# Revit family: Haworth_Masters_StackOnStorage
name_source: partatom
category: Furniture Systems
revit_build: Autodesk Revit 2018 (Build: 20170223_1515(x64)
units: mm (PartAtom-declared; Revit-internal decimal feet)

## family parameters
Always vertical = Yes
Cut with Voids When Loaded = No
OmniClass Number = 23.40.70.14.64.21
OmniClass Title = Systems Furniture
Part Type = Normal
Room Calculation Point = No
Round Connector Dimension = Use Diameter
Shared = No
Work Plane-Based = No

## types (2) — shared parameters
Actual Width = 36"
Assembly Code = E2020200
Bar Pull = Yes
Cabinet Finish = Haworth _ Wood _ White Oak
Classic Pull = No
Custom Size = No
Description = Haworth - Masters - Stack On Storage
Door Finish = Haworth _ Wood _ White Oak
Door Pull Centerline = 20"
Door Width = 17 15/16"
Glass Finish = Haworth _ Glass _ Clear
Linear Pull = No
Manufacturer = Haworth
Max. Width = 36"
Min. Width = 30"
Model = Haworth - Masters - Stack On Storage
Open = No
Pull Finish = Haworth _ Metal _ Brushed Aluminum
Revision Number = 3
Size = Verify Final Dim. w/ Haworth
Standard Widths = 30, 36 in.
Sustainability Info = http://www.haworth.com
Touch Latch = No
URL = www.haworth.com
URL - Product = http://www.haworth.com
Warranty = http://www.haworth.com
Width = 36"
not Open = Yes

## per-type parameters (varying)
| type | Actual Depth | Actual Height | Door Height | Four High | Glass Doors | Legal Depth | Letter Depth | Solid Doors |
| Three High | 16 1/2" | 40" | 40" | No | No | Yes | No | Yes |
| Four High | 14" | 58 1/2" | 58 1/2" | Yes | Yes | No | Yes | No |

type visibility flags (boolean, named after types; folded from table):
- Three High: Yes: Three High
- Four High: Yes: (none)

## geometry (parser evidence)
native form markers: Sweep x10
no freeform markers — native parametric forms only
